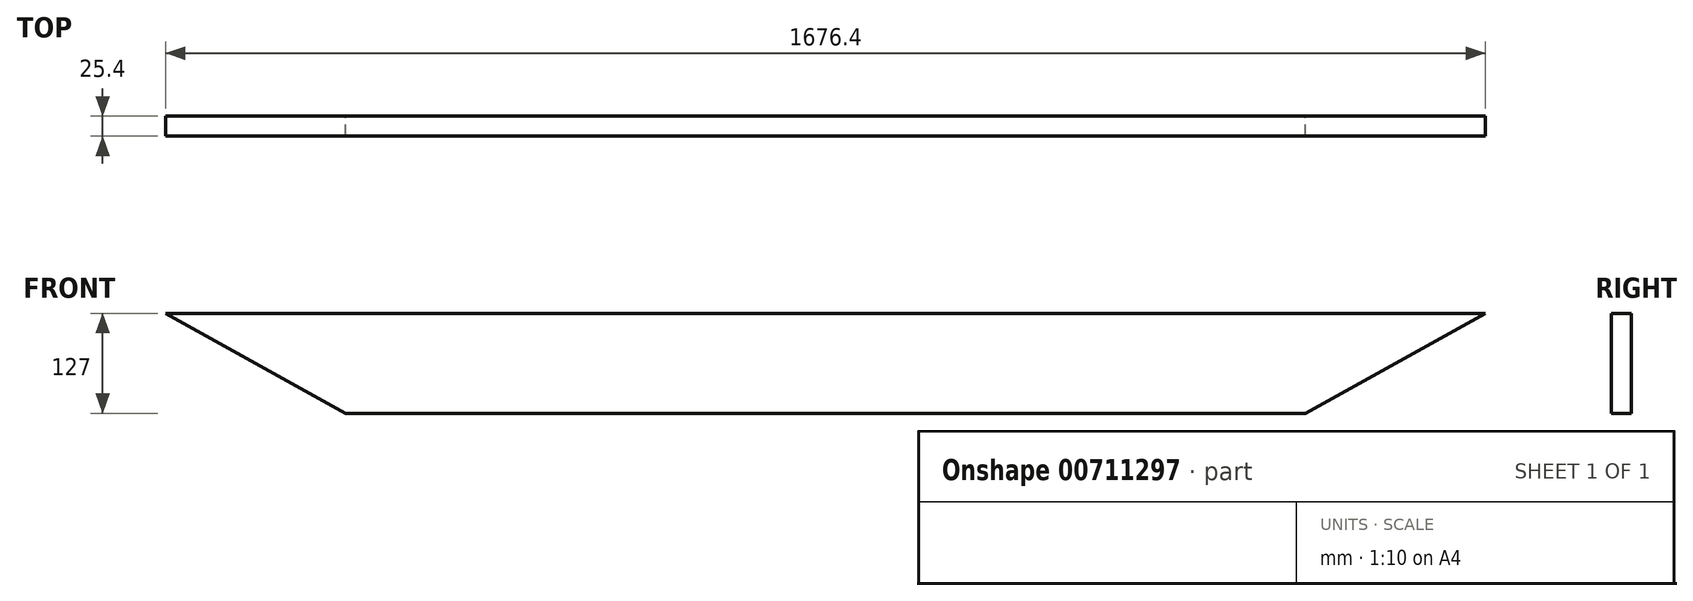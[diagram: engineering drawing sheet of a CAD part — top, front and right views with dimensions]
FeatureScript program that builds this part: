
annotation { "Feature Type Name" : "Feature", "Feature Type Description" : "" }
export const myFeature = defineFeature(function(context is Context, id is Id, definition is map)
    precondition{}
    {
        {
            var Q0;
            Q0=qCreatedBy(makeId("Front.planeOp"),FACE);
            var sketch = newSketch(context, id + "F0", { "sketchPlane" : qUnion([Q0])});
            skLineSegment(sketch, "E0", {"start": v(-777.55, 52.88) * mm, "end": v(898.85, 52.88) * mm});
            skLineSegment(sketch, "E1", {"start": v(-548.95, -74.12) * mm, "end": v(670.25, -74.12) * mm});
            skLineSegment(sketch, "E2", {"start": v(-777.55, 52.88) * mm, "end": v(-548.95, -74.12) * mm});
            skLineSegment(sketch, "E3", {"start": v(898.85, 52.88) * mm, "end": v(670.25, -74.12) * mm});
            skSolve(sketch);
        }
        {
            var Q0;
            Q0 = qSketchRegion(id + "F0", true);
            extrude(context, id + "F1", {"entities" : qUnion([Q0]), "endBound" : BoundingType.SYMMETRIC, "depth" : 25.4 * mm, "offsetDistance" : 25.4 * mm});
        }
    });
